# Revit family: Módulo para control de señales_Aguilera Electronica
name_source: partatom
category: Dispositivos de alarma de incendios
revit_build: Autodesk Revit 2017 (Build: 20160225_1515(x64)
units: mm (PartAtom-declared; Revit-internal decimal feet)

## family parameters
Anfitrión = Cara
Compartido = No
Corte con vacíos al cargar = No
Cota de conector redondo = Diámetro de uso
Mantener orientación de anotación = Sí
Número OmniClass = 23.85.30.21
Punto de cálculo de habitación = No
Tipo de pieza = Normal
Título OmniClass = Environmental Detection/Registration

## types (2) — shared parameters
Diámetro tubo = 20 mm  [stored 0.0656168 ft]
Elevación por defecto = 1200 mm
Fabricante = Aguilera Electrónica
Símbolo = Sí
Símbolo texto modelo = Sí
URL = http://aguilera.es

## per-type parameters (varying)
| type | 2 entradas | 8 entradas | Descripción | Modelo |
| Módulo de 2 entradas para control de señales | Sí | No | Unidad microprocesada direccionable fabricada por AGUILERA ELECTRÓNICA según norma EN 54-
18 que gestiona la información de dos entradas digitales.
Apto para personalizar dos equipos, definir su ubicación y los cambios de estado en cada uno de ellos.
Permite el control independiente en cada entrada y sus contactos son selecionables normalmente
abierto o normalmente cerrado.
Posee las mismas características que el modelo AE/SA-8E. | AE/SA-2E |
| Módulo de 8 entradas para control de señales | No | Sí | Unidad microprocesada direccionable fabricada por AGUILERA ELECTRÓNICA según norma EN 54-18:2003
que gestiona la información de ocho entradas digitales.
Con capacidad para personalizar hasta ocho equipos, identificar su ubicación e informar de los cambios
de estado que se generen en cada uno de ellos. Cada entrada puede ser seleccionada para contacto
abierto o cerrado.
• Provisto de autoaislador que le aísla del resto de la instalación en caso de cortocircuito en su interior.
• Conexión a 2 hilos con clemas extraíbles.
• Alimentación: entre 18 y 27 Vcc.
• Consumo: 1,1 mA en reposo y 1,3mA con las ocho entradas activadas.
• Montado en caja de ABS de 105 x 82 x 25mm. | AE/SA-8E |

note: [stored X ft] marks values corroborated as IEEE doubles in the binary element streams (Revit-internal decimal feet)
